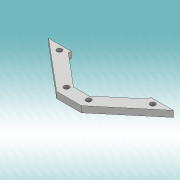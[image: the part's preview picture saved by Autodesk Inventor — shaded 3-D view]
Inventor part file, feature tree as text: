
AUTODESK INVENTOR PART (.ipt)
format: ipt  version: 2019 (Build 230136000, 136)  size: 119,296 bytes
history: native  units: mm
features: extrude x1, sketch x1
ambient origin geometry x8: Origin, YZ Plane, XZ Plane, XY Plane, X Axis, Y Axis, Z Axis, Center Point
bodies: Solid1 (feature_tree)
feature tree (2):
  extrude  "Extrusion1"  Depth=20.5mm
  sketch  "Sketch1"  dims[d6=6.0mm d8=6.981317mm d9=11.0mm d10=6.0mm d12=2.5mm d15=2.4mm d16=3.3mm d17=2.4mm d18=4.2mm d19=3.0mm d20=0.0mm d21=6.0mm d22=20.5mm]
